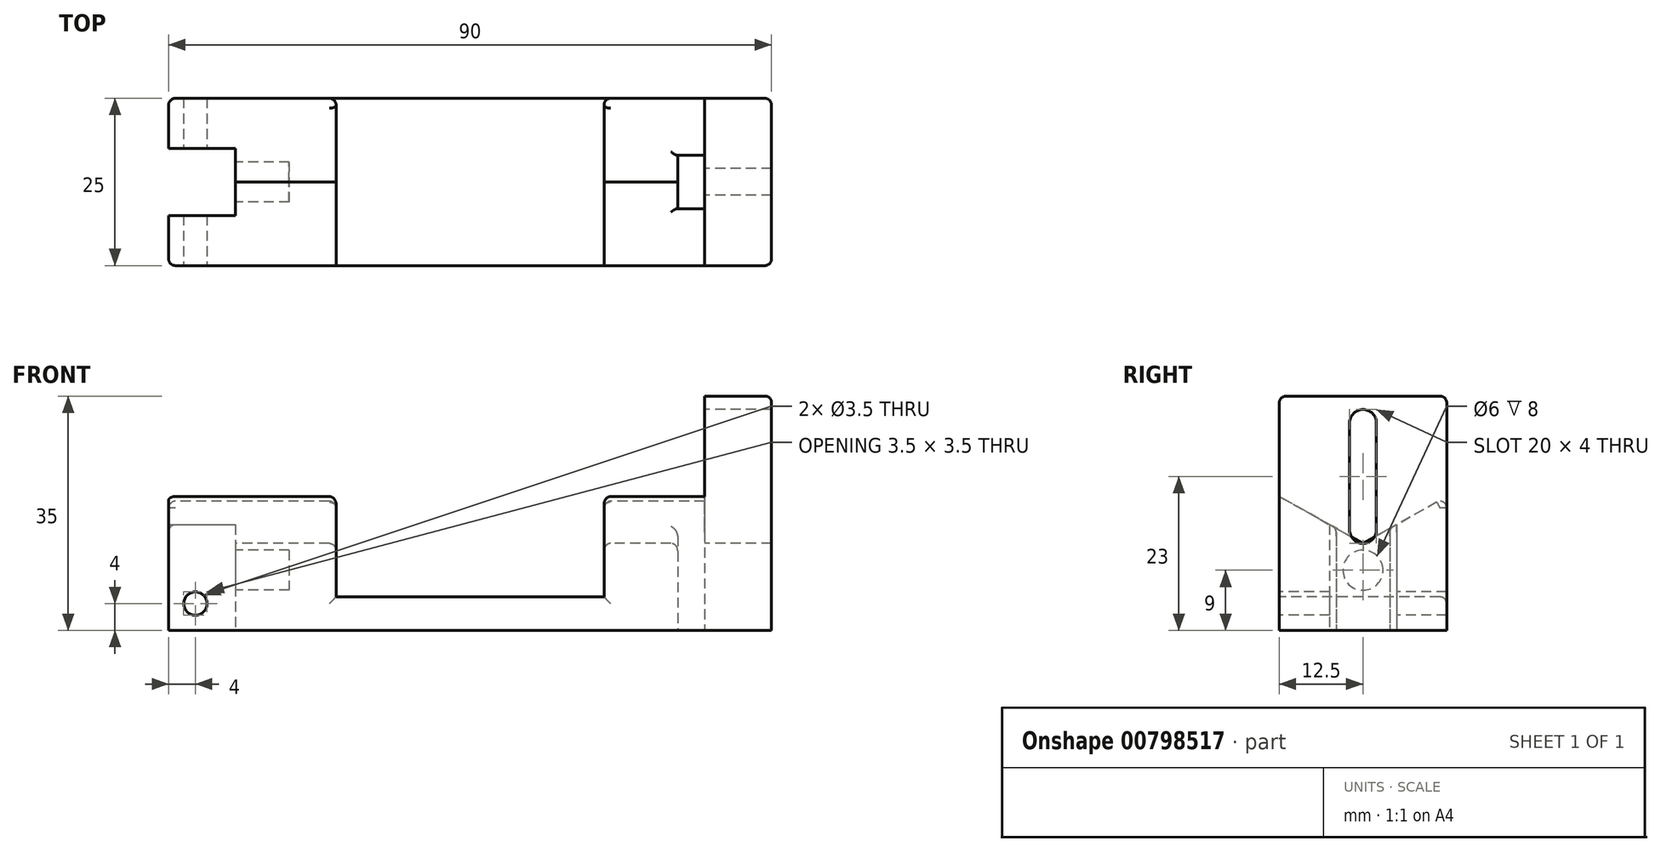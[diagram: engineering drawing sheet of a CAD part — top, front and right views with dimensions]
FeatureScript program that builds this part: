
annotation { "Feature Type Name" : "Feature", "Feature Type Description" : "" }
export const myFeature = defineFeature(function(context is Context, id is Id, definition is map)
    precondition{}
    {
        {
            var Q0;
            Q0=qCreatedBy(makeId("Top.planeOp"),FACE);
            var sketch = newSketch(context, id + "F0", { "sketchPlane" : qUnion([Q0])});
            skLineSegment(sketch, "E0.bottom", {"start": v(45, -12.5) * mm, "end": v(-45, -12.5) * mm});
            skLineSegment(sketch, "E0.top", {"start": v(45, 12.5) * mm, "end": v(-45, 12.5) * mm});
            skLineSegment(sketch, "E0.left", {"start": v(45, -12.5) * mm, "end": v(45, 12.5) * mm});
            skLineSegment(sketch, "E0.right", {"start": v(-45, -12.5) * mm, "end": v(-45, 12.5) * mm});
            skPoint(sketch, "E0.middle", {"position": v(0, 0) * mm});
            skLineSegment(sketch, "E1", {"start": v(45, 12.5) * mm, "end": v(33, 12.5) * mm, "construction": true});
            skLineSegment(sketch, "E2", {"start": v(33, 12.5) * mm, "end": v(33, -12.5) * mm, "construction": true});
            skLineSegment(sketch, "E3.bottom", {"start": v(35, -4) * mm, "end": v(31, -4) * mm});
            skLineSegment(sketch, "E3.top", {"start": v(35, 4) * mm, "end": v(31, 4) * mm});
            skLineSegment(sketch, "E3.left", {"start": v(35, -4) * mm, "end": v(35, 4) * mm});
            skLineSegment(sketch, "E3.right", {"start": v(31, -4) * mm, "end": v(31, 4) * mm});
            skPoint(sketch, "E3.middle", {"position": v(33, 0) * mm});
            skSolve(sketch);
        }
        {
            var Q0;
            Q0 = qSketchRegion(id + "F0", true);
            extrude(context, id + "F1", {"entities" : qUnion([Q0]), "depth" : 35 * mm, "offsetDistance" : 25 * mm});
        }
        {
            var Q0;
            Q0=makeQuery(id+"F1.opExtrude","SWEPT_FACE",FACE,{"disambiguationData":[OSD([sQuery(id+"F0.wireOp",EDGE,"E0.right")])]});
            var sketch = newSketch(context, id + "F2", { "sketchPlane" : qUnion([Q0])});
            skLineSegment(sketch, "E4", {"start": v(-12.5, 35) * mm, "end": v(-12.5, 20) * mm, "construction": true});
            skLineSegment(sketch, "E5", {"start": v(12.5, 35) * mm, "end": v(12.5, 20) * mm, "construction": true});
            skLineSegment(sketch, "E6", {"start": v(0, 35) * mm, "end": v(0, 13) * mm, "construction": true});
            skLineSegment(sketch, "E7", {"start": v(-12.5, 20) * mm, "end": v(0, 13) * mm});
            skLineSegment(sketch, "E8", {"start": v(0, 13) * mm, "end": v(12.5, 20) * mm});
            skLineSegment(sketch, "E9", {"start": v(12.5, 20) * mm, "end": v(12.5, 35) * mm});
            skLineSegment(sketch, "E10", {"start": v(12.5, 35) * mm, "end": v(-12.5, 35) * mm});
            skLineSegment(sketch, "E11", {"start": v(-12.5, 35) * mm, "end": v(-12.5, 20) * mm});
            skSolve(sketch);
        }
        {
            var Q0;
            Q0=makeQuery(id+"F2.imprint","IMPRINT",FACE,{"disambiguationData":[TD([[makeQuery(id+"F2.imprint","IMPRINT",EDGE,{"derivedFrom":sQuery(id+"F2.wireOp",EDGE,"E7")}),1.0]])]});
            extrude(context, id + "F3", {"entities" : qUnion([Q0]), "operationType" : NewBodyOperationType.REMOVE, "oppositeDirection" : true, "depth" : 80 * mm, "offsetDistance" : 25 * mm});
        }
        {
            var Q0;
            Q0=makeQuery(id+"F1.opExtrude","SWEPT_FACE",FACE,{"disambiguationData":[OSD([sQuery(id+"F0.wireOp",EDGE,"E0.bottom")])]});
            var sketch = newSketch(context, id + "F4", { "sketchPlane" : qUnion([Q0])});
            skLineSegment(sketch, "E12", {"start": v(0, 20) * mm, "end": v(-20, 20) * mm, "construction": true});
            skLineSegment(sketch, "E13", {"start": v(-20, 20) * mm, "end": v(-20, 5) * mm, "construction": true});
            skLineSegment(sketch, "E14.MirrorCS", {"start": v(0, 20) * mm, "end": v(20, 20) * mm, "construction": true});
            skLineSegment(sketch, "E15.MirrorCS", {"start": v(20, 20) * mm, "end": v(20, 5) * mm, "construction": true});
            skLineSegment(sketch, "E16.bottom", {"start": v(-20, 20) * mm, "end": v(20, 20) * mm});
            skLineSegment(sketch, "E16.top", {"start": v(-20, 5) * mm, "end": v(20, 5) * mm});
            skLineSegment(sketch, "E16.left", {"start": v(-20, 20) * mm, "end": v(-20, 5) * mm});
            skLineSegment(sketch, "E16.right", {"start": v(20, 20) * mm, "end": v(20, 5) * mm});
            skLineSegment(sketch, "E17", {"start": v(-45, 0) * mm, "end": v(-45, 4) * mm, "construction": true});
            skLineSegment(sketch, "E18", {"start": v(-45, 4) * mm, "end": v(-41, 4) * mm, "construction": true});
            skCircle(sketch, "E19", {"center": v(-41, 4) * mm, "radius": 1.75 * mm});
            skSolve(sketch);
        }
        {
            var Q0;
            Q0=makeQuery(id+"F4.imprint","IMPRINT",FACE,{"disambiguationData":[TD([[makeQuery(id+"F4.imprint","IMPRINT",EDGE,{"derivedFrom":sQuery(id+"F4.wireOp",EDGE,"E19")}),1.0]])]});
            var Q1;
            Q1=makeQuery(id+"F4.imprint","IMPRINT",FACE,{"disambiguationData":[TD([[makeQuery(id+"F4.imprint","IMPRINT",EDGE,{"derivedFrom":sQuery(id+"F4.wireOp",EDGE,"E16.bottom")}),1.0]])]});
            extrude(context, id + "F5", {"entities" : qUnion([Q0, Q1]), "operationType" : NewBodyOperationType.REMOVE, "endBound" : BoundingType.THROUGH_ALL, "oppositeDirection" : true, "depth" : 25 * mm, "offsetDistance" : 25 * mm});
        }
        {
            var Q0;
            Q0=makeQuery(id+"F1.opExtrude","CAP_FACE",FACE,{"disambiguationData":[OSD([sQuery(id+"F0.wireOp",EDGE,"E0.bottom"),sQuery(id+"F0.wireOp",EDGE,"E0.top"),sQuery(id+"F0.wireOp",EDGE,"E0.left"),sQuery(id+"F0.wireOp",EDGE,"E0.right")])],"isStart":true});
            var sketch = newSketch(context, id + "F6", { "sketchPlane" : qUnion([Q0])});
            skLineSegment(sketch, "E20", {"start": v(-45, 0) * mm, "end": v(-35, 0) * mm, "construction": true});
            skLineSegment(sketch, "E21", {"start": v(-35, 0) * mm, "end": v(-35, 5) * mm, "construction": true});
            skLineSegment(sketch, "E22", {"start": v(-45, 0) * mm, "end": v(-45, -5) * mm, "construction": true});
            skLineSegment(sketch, "E23.MirrorCS", {"start": v(-35, 0) * mm, "end": v(-35, -5) * mm, "construction": true});
            skLineSegment(sketch, "E24.MirrorCS", {"start": v(-45, 0) * mm, "end": v(-45, 5) * mm, "construction": true});
            skLineSegment(sketch, "E25.bottom", {"start": v(-45, 5) * mm, "end": v(-35, 5) * mm});
            skLineSegment(sketch, "E25.top", {"start": v(-45, -5) * mm, "end": v(-35, -5) * mm});
            skLineSegment(sketch, "E25.left", {"start": v(-45, 5) * mm, "end": v(-45, -5) * mm});
            skLineSegment(sketch, "E25.right", {"start": v(-35, 5) * mm, "end": v(-35, -5) * mm});
            skSolve(sketch);
        }
        {
            var Q0;
            Q0=makeQuery(id+"F6.imprint","IMPRINT",FACE,{"disambiguationData":[TD([[makeQuery(id+"F6.imprint","IMPRINT",EDGE,{"derivedFrom":sQuery(id+"F6.wireOp",EDGE,"E25.bottom")}),-1.0]])]});
            extrude(context, id + "F7", {"entities" : qUnion([Q0]), "operationType" : NewBodyOperationType.REMOVE, "endBound" : BoundingType.THROUGH_ALL, "oppositeDirection" : true, "depth" : 25 * mm, "offsetDistance" : 25 * mm});
        }
        {
            var Q0;
            Q0=makeQuery(id+"F7.boolean.opBoolean","COPY",FACE,{"derivedFrom":makeQuery(id+"F7.opExtrude","SWEPT_FACE",FACE,{"disambiguationData":[OSD([sQuery(id+"F6.wireOp",EDGE,"E25.right")])]})});
            var sketch = newSketch(context, id + "F8", { "sketchPlane" : qUnion([Q0])});
            skLineSegment(sketch, "E26", {"start": v(0, 0) * mm, "end": v(0, 9) * mm, "construction": true});
            skCircle(sketch, "E27", {"center": v(0, 9) * mm, "radius": 3 * mm});
            skSolve(sketch);
        }
        {
            var Q0;
            {var subQ0=sQuery(id+"F8.wireOp",EDGE,"E27");var subQ1=makeQuery(id+"F7.opExtrude","SWEPT_FACE",FACE,{"disambiguationData":[OSD([sQuery(id+"F6.wireOp",EDGE,"E25.right")])]});var subQ4=makeQuery(id+"F1.opExtrude","SWEPT_FACE",FACE,{"disambiguationData":[OSD([sQuery(id+"F0.wireOp",EDGE,"E0.right")])]});var subQ7=makeQuery(id+"F3.boolean.opBoolean","COPY",FACE,{"derivedFrom":makeQuery(id+"F3.opExtrude","SWEPT_FACE",FACE,{"disambiguationData":[OSD([sQuery(id+"F2.wireOp",EDGE,"E7")])]})});var subQ8=makeQuery(id+"F7.boolean.opBoolean","INTERSECT",EDGE,{"derivedFrom":[makeQuery(id+"F5.boolean.opBoolean","SPLIT",FACE,{"disambiguationData":[TD([subQ4])],"derivedFrom":subQ7}),subQ1]});var subQ9=makeQuery(id+"F8.imprint","INTERSECT",VERTEX,{"derivedFrom":[subQ8,subQ0]});Q0=makeQuery(id+"F8.imprint","IMPRINT",FACE,{"disambiguationData":[TD([[makeQuery(id+"F8.imprint","IMPRINT",EDGE,{"disambiguationData":[TD([[subQ9,-1.0]])],"derivedFrom":subQ0}),1.0]])]});}
            extrude(context, id + "F9", {"entities" : qUnion([Q0]), "operationType" : NewBodyOperationType.REMOVE, "oppositeDirection" : true, "depth" : 8 * mm, "offsetDistance" : 25 * mm});
        }
        {
            var Q0;
            Q0=makeQuery(id+"F0.imprint","IMPRINT",FACE,{"disambiguationData":[TD([[makeQuery(id+"F0.imprint","IMPRINT",EDGE,{"derivedFrom":sQuery(id+"F0.wireOp",EDGE,"E3.bottom")}),-1.0]])]});
            extrude(context, id + "F10", {"entities" : qUnion([Q0]), "operationType" : NewBodyOperationType.REMOVE, "endBound" : BoundingType.THROUGH_ALL, "oppositeDirection" : true, "depth" : 15 * mm, "offsetDistance" : 25 * mm});
        }
        {
            var Q0;
            Q0=makeQuery(id+"F3.boolean.opBoolean","MERGE",FACE,{"derivedFrom":[makeQuery(id+"F1.opExtrude","SWEPT_FACE",FACE,{"disambiguationData":[OSD([sQuery(id+"F0.wireOp",EDGE,"E3.left")])]}),makeQuery(id+"F3.opExtrude","CAP_FACE",FACE,{"disambiguationData":[OSD([sQuery(id+"F2.wireOp",EDGE,"E7"),sQuery(id+"F2.wireOp",EDGE,"E8"),sQuery(id+"F2.wireOp",EDGE,"E9"),sQuery(id+"F2.wireOp",EDGE,"E10"),sQuery(id+"F2.wireOp",EDGE,"E11")])],"isStart":false})]});
            var sketch = newSketch(context, id + "F11", { "sketchPlane" : qUnion([Q0])});
            skLineSegment(sketch, "E28", {"start": v(0, 35) * mm, "end": v(0, 31) * mm, "construction": true});
            skLineSegment(sketch, "E29", {"start": v(0, 31) * mm, "end": v(0, 15) * mm, "construction": true});
            skCircle(sketch, "E30", {"center": v(0, 31) * mm, "radius": 2 * mm});
            skCircle(sketch, "E31", {"center": v(0, 15) * mm, "radius": 2 * mm});
            skLineSegment(sketch, "E32", {"start": v(-2, 31) * mm, "end": v(-2, 15) * mm});
            skLineSegment(sketch, "E33", {"start": v(2, 15) * mm, "end": v(2, 31) * mm});
            skSolve(sketch);
        }
        {
            var Q0;
            {var subQ0=sQuery(id+"F11.wireOp",EDGE,"E30");var subQ1=makeQuery(id+"F11.imprint","INTERSECT",VERTEX,{"derivedFrom":[subQ0,sQuery(id+"F11.wireOp",EDGE,"E32")]});Q0=makeQuery(id+"F11.imprint","IMPRINT",FACE,{"disambiguationData":[TD([[makeQuery(id+"F11.imprint","IMPRINT",EDGE,{"disambiguationData":[TD([[subQ1,1.0]])],"derivedFrom":subQ0}),1.0]])]});}
            var Q1;
            {var subQ0=sQuery(id+"F11.wireOp",EDGE,"E32");Q1=makeQuery(id+"F11.imprint","IMPRINT",FACE,{"disambiguationData":[TD([[makeQuery(id+"F11.imprint","IMPRINT",EDGE,{"derivedFrom":subQ0}),1.0]])]});}
            var Q2;
            {var subQ0=sQuery(id+"F11.wireOp",EDGE,"E31");var subQ1=makeQuery(id+"F11.imprint","INTERSECT",VERTEX,{"derivedFrom":[subQ0,sQuery(id+"F11.wireOp",EDGE,"E32")]});Q2=makeQuery(id+"F11.imprint","IMPRINT",FACE,{"disambiguationData":[TD([[makeQuery(id+"F11.imprint","IMPRINT",EDGE,{"disambiguationData":[TD([[subQ1,1.0]])],"derivedFrom":subQ0}),1.0]])]});}
            extrude(context, id + "F12", {"entities" : qUnion([Q0, Q1, Q2]), "operationType" : NewBodyOperationType.REMOVE, "endBound" : BoundingType.THROUGH_ALL, "oppositeDirection" : true, "depth" : 25 * mm, "offsetDistance" : 25 * mm});
        }
        {
            var Q0;
            {var subQ0=sQuery(id+"F0.wireOp",EDGE,"E0.top");var subQ1=sQuery(id+"F0.wireOp",EDGE,"E0.right");var subQ2=sQuery(id+"F2.wireOp",EDGE,"E7");Q0=makeQuery(id+"F5.boolean.opBoolean","SPLIT",EDGE,{"disambiguationData":[TD([makeQuery(id+"F1.opExtrude","SWEPT_FACE",FACE,{"disambiguationData":[OSD([subQ1])]})])],"derivedFrom":makeQuery(id+"F3.boolean.opBoolean","COPY",EDGE,{"derivedFrom":makeQuery(id+"F3.opExtrude","SWEPT_EDGE",EDGE,{"disambiguationData":[OSD([subQ0,subQ1,subQ2,sQuery(id+"F2.wireOp",EDGE,"E11")])]})})});}
            var Q1;
            {var subQ0=sQuery(id+"F0.wireOp",EDGE,"E0.bottom");var subQ1=sQuery(id+"F0.wireOp",EDGE,"E0.right");var subQ2=sQuery(id+"F2.wireOp",EDGE,"E8");Q1=makeQuery(id+"F5.boolean.opBoolean","SPLIT",EDGE,{"disambiguationData":[TD([makeQuery(id+"F1.opExtrude","SWEPT_FACE",FACE,{"disambiguationData":[OSD([subQ1])]})])],"derivedFrom":makeQuery(id+"F3.boolean.opBoolean","COPY",EDGE,{"derivedFrom":makeQuery(id+"F3.opExtrude","SWEPT_EDGE",EDGE,{"disambiguationData":[OSD([subQ0,subQ1,subQ2,sQuery(id+"F2.wireOp",EDGE,"E9")])]})})});}
            var Q2;
            {var subQ0=sQuery(id+"F2.wireOp",EDGE,"E8");var subQ1=sQuery(id+"F2.wireOp",EDGE,"E9");var subQ2=sQuery(id+"F0.wireOp",EDGE,"E0.bottom");Q2=makeQuery(id+"F5.boolean.opBoolean","SPLIT",EDGE,{"disambiguationData":[TD([makeQuery(id+"F1.opExtrude","SWEPT_FACE",FACE,{"disambiguationData":[OSD([sQuery(id+"F0.wireOp",EDGE,"E3.left")])]})])],"derivedFrom":makeQuery(id+"F3.boolean.opBoolean","COPY",EDGE,{"derivedFrom":makeQuery(id+"F3.opExtrude","SWEPT_EDGE",EDGE,{"disambiguationData":[OSD([subQ2,sQuery(id+"F0.wireOp",EDGE,"E0.right"),subQ0,subQ1])]})})});}
            var Q3;
            {var subQ0=sQuery(id+"F2.wireOp",EDGE,"E7");var subQ1=sQuery(id+"F2.wireOp",EDGE,"E11");var subQ2=sQuery(id+"F0.wireOp",EDGE,"E0.top");Q3=makeQuery(id+"F5.boolean.opBoolean","SPLIT",EDGE,{"disambiguationData":[TD([makeQuery(id+"F1.opExtrude","SWEPT_FACE",FACE,{"disambiguationData":[OSD([sQuery(id+"F0.wireOp",EDGE,"E3.left")])]})])],"derivedFrom":makeQuery(id+"F3.boolean.opBoolean","COPY",EDGE,{"derivedFrom":makeQuery(id+"F3.opExtrude","SWEPT_EDGE",EDGE,{"disambiguationData":[OSD([subQ2,sQuery(id+"F0.wireOp",EDGE,"E0.right"),subQ0,subQ1])]})})});}
            var Q4;
            Q4=makeQuery(id+"F5.boolean.opBoolean","INTERSECT",EDGE,{"derivedFrom":[makeQuery(id+"F3.boolean.opBoolean","COPY",FACE,{"derivedFrom":makeQuery(id+"F3.opExtrude","SWEPT_FACE",FACE,{"disambiguationData":[OSD([sQuery(id+"F2.wireOp",EDGE,"E7")])]})}),makeQuery(id+"F5.opExtrude","SWEPT_FACE",FACE,{"disambiguationData":[OSD([sQuery(id+"F4.wireOp",EDGE,"E16.right")])]})]});
            var Q5;
            Q5=makeQuery(id+"F5.boolean.opBoolean","INTERSECT",EDGE,{"derivedFrom":[makeQuery(id+"F3.boolean.opBoolean","COPY",FACE,{"derivedFrom":makeQuery(id+"F3.opExtrude","SWEPT_FACE",FACE,{"disambiguationData":[OSD([sQuery(id+"F2.wireOp",EDGE,"E8")])]})}),makeQuery(id+"F5.opExtrude","SWEPT_FACE",FACE,{"disambiguationData":[OSD([sQuery(id+"F4.wireOp",EDGE,"E16.right")])]})]});
            var Q6;
            Q6=makeQuery(id+"F5.boolean.opBoolean","INTERSECT",EDGE,{"derivedFrom":[makeQuery(id+"F3.boolean.opBoolean","COPY",FACE,{"derivedFrom":makeQuery(id+"F3.opExtrude","SWEPT_FACE",FACE,{"disambiguationData":[OSD([sQuery(id+"F2.wireOp",EDGE,"E7")])]})}),makeQuery(id+"F5.opExtrude","SWEPT_FACE",FACE,{"disambiguationData":[OSD([sQuery(id+"F4.wireOp",EDGE,"E16.left")])]})]});
            var Q7;
            Q7=makeQuery(id+"F3.boolean.opBoolean","COPY",EDGE,{"derivedFrom":makeQuery(id+"F3.opExtrude","CAP_EDGE",EDGE,{"disambiguationData":[OSD([sQuery(id+"F2.wireOp",EDGE,"E7")])],"isStart":true})});
            var Q8;
            Q8=makeQuery(id+"F5.boolean.opBoolean","INTERSECT",EDGE,{"derivedFrom":[makeQuery(id+"F3.boolean.opBoolean","COPY",FACE,{"derivedFrom":makeQuery(id+"F3.opExtrude","SWEPT_FACE",FACE,{"disambiguationData":[OSD([sQuery(id+"F2.wireOp",EDGE,"E8")])]})}),makeQuery(id+"F5.opExtrude","SWEPT_FACE",FACE,{"disambiguationData":[OSD([sQuery(id+"F4.wireOp",EDGE,"E16.left")])]})]});
            var Q9;
            Q9=makeQuery(id+"F3.boolean.opBoolean","COPY",EDGE,{"derivedFrom":makeQuery(id+"F3.opExtrude","CAP_EDGE",EDGE,{"disambiguationData":[OSD([sQuery(id+"F2.wireOp",EDGE,"E8")])],"isStart":true})});
            var Q10;
            Q10=makeQuery(id+"F1.opExtrude","SWEPT_EDGE",EDGE,{"disambiguationData":[OSD([sQuery(id+"F0.wireOp",EDGE,"E0.bottom"),sQuery(id+"F0.wireOp",EDGE,"E0.right")])]});
            var Q11;
            Q11=makeQuery(id+"F1.opExtrude","SWEPT_EDGE",EDGE,{"disambiguationData":[OSD([sQuery(id+"F0.wireOp",EDGE,"E0.top"),sQuery(id+"F0.wireOp",EDGE,"E0.right")])]});
            var Q12;
            Q12=makeQuery(id+"F1.opExtrude","SWEPT_EDGE",EDGE,{"disambiguationData":[OSD([sQuery(id+"F0.wireOp",EDGE,"E0.bottom"),sQuery(id+"F0.wireOp",EDGE,"E0.left")])]});
            var Q13;
            Q13=makeQuery(id+"F1.opExtrude","SWEPT_EDGE",EDGE,{"disambiguationData":[OSD([sQuery(id+"F0.wireOp",EDGE,"E0.top"),sQuery(id+"F0.wireOp",EDGE,"E0.left")])]});
            var Q14;
            Q14=makeQuery(id+"F1.opExtrude","CAP_EDGE",EDGE,{"disambiguationData":[OSD([sQuery(id+"F0.wireOp",EDGE,"E0.left")])],"isStart":false});
            var Q15;
            Q15=makeQuery(id+"F1.opExtrude","CAP_EDGE",EDGE,{"disambiguationData":[OSD([sQuery(id+"F0.wireOp",EDGE,"E0.bottom")])],"isStart":false});
            var Q16;
            Q16=makeQuery(id+"F3.boolean.opBoolean","MERGE",EDGE,{"derivedFrom":[makeQuery(id+"F1.opExtrude","CAP_EDGE",EDGE,{"disambiguationData":[OSD([sQuery(id+"F0.wireOp",EDGE,"E3.left")])],"isStart":false}),makeQuery(id+"F3.opExtrude","CAP_EDGE",EDGE,{"disambiguationData":[OSD([sQuery(id+"F2.wireOp",EDGE,"E10")])],"isStart":false})]});
            var Q17;
            Q17=makeQuery(id+"F1.opExtrude","CAP_EDGE",EDGE,{"disambiguationData":[OSD([sQuery(id+"F0.wireOp",EDGE,"E0.top")])],"isStart":false});
            var Q18;
            Q18=makeQuery(id+"F3.boolean.opBoolean","COPY",EDGE,{"derivedFrom":makeQuery(id+"F3.opExtrude","CAP_EDGE",EDGE,{"disambiguationData":[OSD([sQuery(id+"F2.wireOp",EDGE,"E9")])],"isStart":false})});
            var Q19;
            Q19=makeQuery(id+"F3.boolean.opBoolean","COPY",EDGE,{"derivedFrom":makeQuery(id+"F3.opExtrude","CAP_EDGE",EDGE,{"disambiguationData":[OSD([sQuery(id+"F2.wireOp",EDGE,"E11")])],"isStart":false})});
            fillet(context, id + "F13", {"entities" : qUnion([Q0, Q1, Q2, Q3, Q4, Q5, Q6, Q7, Q8, Q9, Q10, Q11, Q12, Q13, Q14, Q15, Q16, Q17, Q18, Q19]), "radius" : 1 * mm, "tangentPropagation" : true, "allowEdgeOverflow" : false});
        }
        {
            var Q0;
            Q0=makeQuery(id+"F5.boolean.opBoolean","COPY",EDGE,{"derivedFrom":makeQuery(id+"F5.opExtrude","CAP_EDGE",EDGE,{"disambiguationData":[OSD([sQuery(id+"F4.wireOp",EDGE,"E16.left")])],"isStart":true})});
            var Q1;
            Q1=makeQuery(id+"F5.boolean.opBoolean","COPY",EDGE,{"derivedFrom":makeQuery(id+"F5.opExtrude","CAP_EDGE",EDGE,{"disambiguationData":[OSD([sQuery(id+"F4.wireOp",EDGE,"E16.top")])],"isStart":true})});
            var Q2;
            Q2=makeQuery(id+"F5.boolean.opBoolean","COPY",EDGE,{"derivedFrom":makeQuery(id+"F5.opExtrude","CAP_EDGE",EDGE,{"disambiguationData":[OSD([sQuery(id+"F4.wireOp",EDGE,"E16.right")])],"isStart":true})});
            var Q3;
            Q3=makeQuery(id+"F5.boolean.opBoolean","INTERSECT",EDGE,{"derivedFrom":[makeQuery(id+"F1.opExtrude","SWEPT_FACE",FACE,{"disambiguationData":[OSD([sQuery(id+"F0.wireOp",EDGE,"E0.top")])]}),makeQuery(id+"F5.opExtrude","SWEPT_FACE",FACE,{"disambiguationData":[OSD([sQuery(id+"F4.wireOp",EDGE,"E16.top")])]})]});
            var Q4;
            Q4=makeQuery(id+"F5.boolean.opBoolean","INTERSECT",EDGE,{"derivedFrom":[makeQuery(id+"F1.opExtrude","SWEPT_FACE",FACE,{"disambiguationData":[OSD([sQuery(id+"F0.wireOp",EDGE,"E0.top")])]}),makeQuery(id+"F5.opExtrude","SWEPT_FACE",FACE,{"disambiguationData":[OSD([sQuery(id+"F4.wireOp",EDGE,"E16.left")])]})]});
            var Q5;
            Q5=makeQuery(id+"F5.boolean.opBoolean","INTERSECT",EDGE,{"derivedFrom":[makeQuery(id+"F1.opExtrude","SWEPT_FACE",FACE,{"disambiguationData":[OSD([sQuery(id+"F0.wireOp",EDGE,"E0.top")])]}),makeQuery(id+"F5.opExtrude","SWEPT_FACE",FACE,{"disambiguationData":[OSD([sQuery(id+"F4.wireOp",EDGE,"E16.right")])]})]});
            var Q6;
            Q6=makeQuery(id+"F3.boolean.opBoolean","INTERSECT",EDGE,{"derivedFrom":[makeQuery(id+"F1.opExtrude","SWEPT_FACE",FACE,{"disambiguationData":[OSD([sQuery(id+"F0.wireOp",EDGE,"E3.top")])]}),makeQuery(id+"F3.opExtrude","SWEPT_FACE",FACE,{"disambiguationData":[OSD([sQuery(id+"F2.wireOp",EDGE,"E7")])]})]});
            var Q7;
            Q7=makeQuery(id+"F3.boolean.opBoolean","INTERSECT",EDGE,{"derivedFrom":[makeQuery(id+"F1.opExtrude","SWEPT_FACE",FACE,{"disambiguationData":[OSD([sQuery(id+"F0.wireOp",EDGE,"E3.bottom")])]}),makeQuery(id+"F3.opExtrude","SWEPT_FACE",FACE,{"disambiguationData":[OSD([sQuery(id+"F2.wireOp",EDGE,"E8")])]})]});
            var Q8;
            Q8=makeQuery(id+"F3.boolean.opBoolean","INTERSECT",EDGE,{"derivedFrom":[makeQuery(id+"F1.opExtrude","SWEPT_FACE",FACE,{"disambiguationData":[OSD([sQuery(id+"F0.wireOp",EDGE,"E3.right")])]}),makeQuery(id+"F3.opExtrude","SWEPT_FACE",FACE,{"disambiguationData":[OSD([sQuery(id+"F2.wireOp",EDGE,"E8")])]})]});
            var Q9;
            Q9=makeQuery(id+"F3.boolean.opBoolean","INTERSECT",EDGE,{"derivedFrom":[makeQuery(id+"F1.opExtrude","SWEPT_FACE",FACE,{"disambiguationData":[OSD([sQuery(id+"F0.wireOp",EDGE,"E3.right")])]}),makeQuery(id+"F3.opExtrude","SWEPT_FACE",FACE,{"disambiguationData":[OSD([sQuery(id+"F2.wireOp",EDGE,"E7")])]})]});
            fillet(context, id + "F14", {"entities" : qUnion([Q0, Q1, Q2, Q3, Q4, Q5, Q6, Q7, Q8, Q9]), "radius" : 1 * mm, "tangentPropagation" : true, "allowEdgeOverflow" : false});
        }
    });
